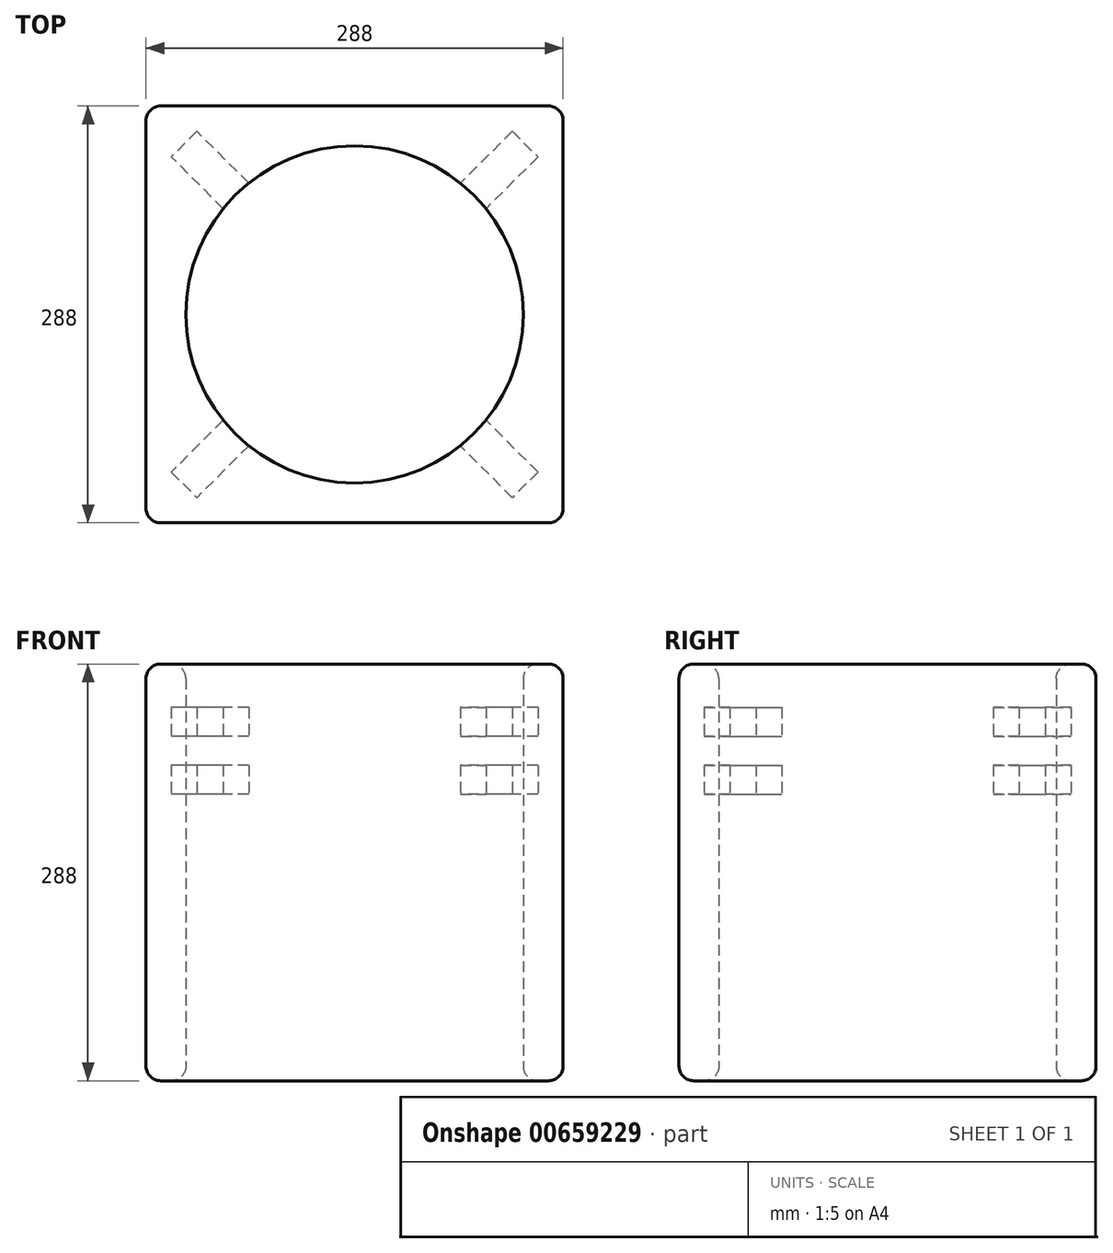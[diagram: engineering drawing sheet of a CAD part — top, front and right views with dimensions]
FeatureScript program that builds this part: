
annotation { "Feature Type Name" : "Feature", "Feature Type Description" : "" }
export const myFeature = defineFeature(function(context is Context, id is Id, definition is map)
    precondition{}
    {
        {
            var Q0;
            Q0=qCreatedBy(makeId("Top.planeOp"),FACE);
            var sketch = newSketch(context, id + "F0", { "sketchPlane" : qUnion([Q0])});
            skCircle(sketch, "E0", {"center": v(0, 0) * mm, "radius": 116.5 * mm});
            skLineSegment(sketch, "E1.bottom", {"start": v(144, 144) * mm, "end": v(-144, 144) * mm});
            skLineSegment(sketch, "E1.top", {"start": v(144, -144) * mm, "end": v(-144, -144) * mm});
            skLineSegment(sketch, "E1.left", {"start": v(144, 144) * mm, "end": v(144, -144) * mm});
            skLineSegment(sketch, "E1.right", {"start": v(-144, 144) * mm, "end": v(-144, -144) * mm});
            skSolve(sketch);
        }
        {
            var Q0;
            Q0=makeQuery(id+"F0.imprint","IMPRINT",FACE,{"disambiguationData":[TD([[makeQuery(id+"F0.imprint","IMPRINT",EDGE,{"derivedFrom":sQuery(id+"F0.wireOp",EDGE,"E0")}),-1.0]])]});
            extrude(context, id + "F1", {"entities" : qUnion([Q0]), "depth" : 288 * mm, "offsetDistance" : 25 * mm});
        }
        {
            var Q0;
            Q0=makeQuery(id+"F1.opExtrude","CAP_FACE",FACE,{"disambiguationData":[OSD([sQuery(id+"F0.wireOp",EDGE,"E0"),sQuery(id+"F0.wireOp",EDGE,"E1.bottom"),sQuery(id+"F0.wireOp",EDGE,"E1.top"),sQuery(id+"F0.wireOp",EDGE,"E1.left"),sQuery(id+"F0.wireOp",EDGE,"E1.right")])],"isStart":false});
            var Q1;
            Q1=makeQuery(id+"F1.opExtrude","CAP_FACE",FACE,{"disambiguationData":[OSD([sQuery(id+"F0.wireOp",EDGE,"E0"),sQuery(id+"F0.wireOp",EDGE,"E1.bottom"),sQuery(id+"F0.wireOp",EDGE,"E1.top"),sQuery(id+"F0.wireOp",EDGE,"E1.left"),sQuery(id+"F0.wireOp",EDGE,"E1.right")])],"isStart":true});
            var Q2;
            {var subQ0=sQuery(id+"F0.wireOp",EDGE,"E1.bottom");Q2=makeQuery(id+"Fkc3ZmtWVtNshut_1.opChamfer","BLEND_EDGE",EDGE,{"blendedFrom":[makeQuery(id+"F1.opExtrude","SWEPT_EDGE",EDGE,{"disambiguationData":[OSD([subQ0,sQuery(id+"F0.wireOp",EDGE,"E1.right")])]}),makeQuery(id+"F1.opExtrude","SWEPT_FACE",FACE,{"disambiguationData":[OSD([subQ0])]})],"blendedInto":[makeQuery(id+"F1.opExtrude","SWEPT_FACE",FACE,{"disambiguationData":[OSD([subQ0])]})]});}
            var Q3;
            Q3=makeQuery(id+"F1.opExtrude","SWEPT_FACE",FACE,{"disambiguationData":[OSD([sQuery(id+"F0.wireOp",EDGE,"E1.right")])]});
            var Q4;
            {var subQ0=sQuery(id+"F0.wireOp",EDGE,"E1.top");Q4=makeQuery(id+"Fkc3ZmtWVtNshut_1.opChamfer","BLEND_EDGE",EDGE,{"blendedFrom":[makeQuery(id+"F1.opExtrude","SWEPT_EDGE",EDGE,{"disambiguationData":[OSD([subQ0,sQuery(id+"F0.wireOp",EDGE,"E1.right")])]}),makeQuery(id+"F1.opExtrude","SWEPT_FACE",FACE,{"disambiguationData":[OSD([subQ0])]})],"blendedInto":[makeQuery(id+"F1.opExtrude","SWEPT_FACE",FACE,{"disambiguationData":[OSD([subQ0])]})]});}
            var Q5;
            {var subQ0=sQuery(id+"F0.wireOp",EDGE,"E1.top");Q5=makeQuery(id+"Fkc3ZmtWVtNshut_1.opChamfer","BLEND_EDGE",EDGE,{"blendedFrom":[makeQuery(id+"F1.opExtrude","SWEPT_EDGE",EDGE,{"disambiguationData":[OSD([subQ0,sQuery(id+"F0.wireOp",EDGE,"E1.left")])]}),makeQuery(id+"F1.opExtrude","SWEPT_FACE",FACE,{"disambiguationData":[OSD([subQ0])]})],"blendedInto":[makeQuery(id+"F1.opExtrude","SWEPT_FACE",FACE,{"disambiguationData":[OSD([subQ0])]})]});}
            var Q6;
            Q6=makeQuery(id+"Fkc3ZmtWVtNshut_1.opChamfer","BLEND_FACE",FACE,{"disambiguationData":[OSD([sQuery(id+"F0.wireOp",EDGE,"E1.top"),sQuery(id+"F0.wireOp",EDGE,"E1.left")])]});
            var Q7;
            Q7=makeQuery(id+"F1.opExtrude","SWEPT_FACE",FACE,{"disambiguationData":[OSD([sQuery(id+"F0.wireOp",EDGE,"E1.left")])]});
            var Q8;
            Q8=makeQuery(id+"Fkc3ZmtWVtNshut_1.opChamfer","BLEND_FACE",FACE,{"disambiguationData":[OSD([sQuery(id+"F0.wireOp",EDGE,"E1.bottom"),sQuery(id+"F0.wireOp",EDGE,"E1.left")])]});
            fillet(context, id + "F2", {"entities" : qUnion([Q0, Q1, Q2, Q3, Q4, Q5, Q6, Q7, Q8]), "radius" : 10 * mm, "tangentPropagation" : true, "allowEdgeOverflow" : false});
        }
        {
            var Q0;
            {var subQ0=sQuery(id+"F0.wireOp",EDGE,"E1.right");var subQ1=sQuery(id+"F0.wireOp",EDGE,"E1.top");Q0=makeQuery(id+"F2.opFillet","BLEND_VERTEX",VERTEX,{"blendedFrom":[makeQuery(id+"F1.opExtrude","CAP_VERTEX",VERTEX,{"disambiguationData":[OSD([subQ1,subQ0])],"isStart":false}),makeQuery(id+"F1.opExtrude","CAP_EDGE",EDGE,{"disambiguationData":[OSD([subQ1])],"isStart":false}),makeQuery(id+"F1.opExtrude","CAP_EDGE",EDGE,{"disambiguationData":[OSD([subQ0])],"isStart":false}),makeQuery(id+"F1.opExtrude","CAP_FACE",FACE,{"disambiguationData":[OSD([sQuery(id+"F0.wireOp",EDGE,"E0"),sQuery(id+"F0.wireOp",EDGE,"E1.bottom"),subQ1,sQuery(id+"F0.wireOp",EDGE,"E1.left"),subQ0])],"isStart":false})],"blendedInto":[makeQuery(id+"F1.opExtrude","CAP_FACE",FACE,{"disambiguationData":[OSD([sQuery(id+"F0.wireOp",EDGE,"E0"),sQuery(id+"F0.wireOp",EDGE,"E1.bottom"),subQ1,sQuery(id+"F0.wireOp",EDGE,"E1.left"),subQ0])],"isStart":false})]});}
            var Q1;
            {var subQ0=sQuery(id+"F0.wireOp",EDGE,"E1.left");var subQ1=sQuery(id+"F0.wireOp",EDGE,"E1.bottom");Q1=makeQuery(id+"F2.opFillet","BLEND_VERTEX",VERTEX,{"blendedFrom":[makeQuery(id+"F1.opExtrude","CAP_VERTEX",VERTEX,{"disambiguationData":[OSD([subQ1,subQ0])],"isStart":false}),makeQuery(id+"F1.opExtrude","CAP_EDGE",EDGE,{"disambiguationData":[OSD([subQ1])],"isStart":false}),makeQuery(id+"F1.opExtrude","CAP_EDGE",EDGE,{"disambiguationData":[OSD([subQ0])],"isStart":false}),makeQuery(id+"F1.opExtrude","CAP_FACE",FACE,{"disambiguationData":[OSD([sQuery(id+"F0.wireOp",EDGE,"E0"),subQ1,sQuery(id+"F0.wireOp",EDGE,"E1.top"),subQ0,sQuery(id+"F0.wireOp",EDGE,"E1.right")])],"isStart":false})],"blendedInto":[makeQuery(id+"F1.opExtrude","CAP_FACE",FACE,{"disambiguationData":[OSD([sQuery(id+"F0.wireOp",EDGE,"E0"),subQ1,sQuery(id+"F0.wireOp",EDGE,"E1.top"),subQ0,sQuery(id+"F0.wireOp",EDGE,"E1.right")])],"isStart":false})]});}
            var Q2;
            {var subQ0=sQuery(id+"F0.wireOp",EDGE,"E1.left");var subQ1=sQuery(id+"F0.wireOp",EDGE,"E1.bottom");Q2=makeQuery(id+"F2.opFillet","BLEND_VERTEX",VERTEX,{"blendedFrom":[makeQuery(id+"F1.opExtrude","CAP_VERTEX",VERTEX,{"disambiguationData":[OSD([subQ1,subQ0])],"isStart":true}),makeQuery(id+"F1.opExtrude","CAP_EDGE",EDGE,{"disambiguationData":[OSD([subQ1])],"isStart":true}),makeQuery(id+"F1.opExtrude","CAP_EDGE",EDGE,{"disambiguationData":[OSD([subQ0])],"isStart":true}),makeQuery(id+"F1.opExtrude","CAP_FACE",FACE,{"disambiguationData":[OSD([sQuery(id+"F0.wireOp",EDGE,"E0"),subQ1,sQuery(id+"F0.wireOp",EDGE,"E1.top"),subQ0,sQuery(id+"F0.wireOp",EDGE,"E1.right")])],"isStart":true})],"blendedInto":[makeQuery(id+"F1.opExtrude","CAP_FACE",FACE,{"disambiguationData":[OSD([sQuery(id+"F0.wireOp",EDGE,"E0"),subQ1,sQuery(id+"F0.wireOp",EDGE,"E1.top"),subQ0,sQuery(id+"F0.wireOp",EDGE,"E1.right")])],"isStart":true})]});}
            cPlane(context, id + "F3", {"entities" : qUnion([Q0, Q1, Q2]), "cplaneType" : CPlaneType.THREE_POINT, "offset" : 25 * mm, "width" : 150 * mm, "height" : 150 * mm});
        }
        {
            var Q0;
            Q0=qCreatedBy(id+"F3.planeOp",FACE);
            var sketch = newSketch(context, id + "F4", { "sketchPlane" : qUnion([Q0])});
            skLineSegment(sketch, "E2.bottom", {"start": v(12.5, 258) * mm, "end": v(-12.5, 258) * mm});
            skLineSegment(sketch, "E2.top", {"start": v(12.5, 238) * mm, "end": v(-12.5, 238) * mm});
            skLineSegment(sketch, "E2.left", {"start": v(12.5, 258) * mm, "end": v(12.5, 238) * mm});
            skLineSegment(sketch, "E2.right", {"start": v(-12.5, 258) * mm, "end": v(-12.5, 238) * mm});
            skPoint(sketch, "E2.middle", {"position": v(0, 248) * mm});
            skLineSegment(sketch, "E3.bottom", {"start": v(12.5, 218) * mm, "end": v(-12.5, 218) * mm});
            skLineSegment(sketch, "E3.top", {"start": v(12.5, 198) * mm, "end": v(-12.5, 198) * mm});
            skLineSegment(sketch, "E3.left", {"start": v(12.5, 218) * mm, "end": v(12.5, 198) * mm});
            skLineSegment(sketch, "E3.right", {"start": v(-12.5, 218) * mm, "end": v(-12.5, 198) * mm});
            skPoint(sketch, "E3.middle", {"position": v(0, 208) * mm});
            skSolve(sketch);
        }
        {
            var Q0;
            Q0=makeQuery(id+"F4.imprint","IMPRINT",FACE,{"disambiguationData":[TD([[makeQuery(id+"F4.imprint","IMPRINT",EDGE,{"derivedFrom":sQuery(id+"F4.wireOp",EDGE,"E2.bottom")}),1.0]])]});
            var Q1;
            Q1=makeQuery(id+"F4.imprint","IMPRINT",FACE,{"disambiguationData":[TD([[makeQuery(id+"F4.imprint","IMPRINT",EDGE,{"derivedFrom":sQuery(id+"F4.wireOp",EDGE,"E3.bottom")}),1.0]])]});
            extrude(context, id + "F5", {"entities" : qUnion([Q0, Q1]), "operationType" : NewBodyOperationType.REMOVE, "depth" : 333 * mm, "offsetDistance" : 25 * mm, "symmetric" : true});
        }
        {
            var Q0;
            {var subQ0=sQuery(id+"F0.wireOp",EDGE,"E1.left");var subQ1=sQuery(id+"F0.wireOp",EDGE,"E1.top");Q0=makeQuery(id+"F2.opFillet","BLEND_VERTEX",VERTEX,{"blendedFrom":[makeQuery(id+"F1.opExtrude","CAP_VERTEX",VERTEX,{"disambiguationData":[OSD([subQ1,subQ0])],"isStart":false}),makeQuery(id+"F1.opExtrude","CAP_EDGE",EDGE,{"disambiguationData":[OSD([subQ1])],"isStart":false}),makeQuery(id+"F1.opExtrude","CAP_EDGE",EDGE,{"disambiguationData":[OSD([subQ0])],"isStart":false}),makeQuery(id+"F1.opExtrude","CAP_FACE",FACE,{"disambiguationData":[OSD([sQuery(id+"F0.wireOp",EDGE,"E0"),sQuery(id+"F0.wireOp",EDGE,"E1.bottom"),subQ1,subQ0,sQuery(id+"F0.wireOp",EDGE,"E1.right")])],"isStart":false})],"blendedInto":[makeQuery(id+"F1.opExtrude","CAP_FACE",FACE,{"disambiguationData":[OSD([sQuery(id+"F0.wireOp",EDGE,"E0"),sQuery(id+"F0.wireOp",EDGE,"E1.bottom"),subQ1,subQ0,sQuery(id+"F0.wireOp",EDGE,"E1.right")])],"isStart":false})]});}
            var Q1;
            {var subQ0=sQuery(id+"F0.wireOp",EDGE,"E1.right");var subQ1=sQuery(id+"F0.wireOp",EDGE,"E1.bottom");Q1=makeQuery(id+"F2.opFillet","BLEND_VERTEX",VERTEX,{"blendedFrom":[makeQuery(id+"F1.opExtrude","CAP_VERTEX",VERTEX,{"disambiguationData":[OSD([subQ1,subQ0])],"isStart":false}),makeQuery(id+"F1.opExtrude","CAP_EDGE",EDGE,{"disambiguationData":[OSD([subQ1])],"isStart":false}),makeQuery(id+"F1.opExtrude","CAP_EDGE",EDGE,{"disambiguationData":[OSD([subQ0])],"isStart":false}),makeQuery(id+"F1.opExtrude","CAP_FACE",FACE,{"disambiguationData":[OSD([sQuery(id+"F0.wireOp",EDGE,"E0"),subQ1,sQuery(id+"F0.wireOp",EDGE,"E1.top"),sQuery(id+"F0.wireOp",EDGE,"E1.left"),subQ0])],"isStart":false})],"blendedInto":[makeQuery(id+"F1.opExtrude","CAP_FACE",FACE,{"disambiguationData":[OSD([sQuery(id+"F0.wireOp",EDGE,"E0"),subQ1,sQuery(id+"F0.wireOp",EDGE,"E1.top"),sQuery(id+"F0.wireOp",EDGE,"E1.left"),subQ0])],"isStart":false})]});}
            var Q2;
            {var subQ0=sQuery(id+"F0.wireOp",EDGE,"E1.right");var subQ1=sQuery(id+"F0.wireOp",EDGE,"E1.bottom");Q2=makeQuery(id+"F2.opFillet","BLEND_VERTEX",VERTEX,{"blendedFrom":[makeQuery(id+"F1.opExtrude","CAP_VERTEX",VERTEX,{"disambiguationData":[OSD([subQ1,subQ0])],"isStart":true}),makeQuery(id+"F1.opExtrude","CAP_EDGE",EDGE,{"disambiguationData":[OSD([subQ1])],"isStart":true}),makeQuery(id+"F1.opExtrude","CAP_EDGE",EDGE,{"disambiguationData":[OSD([subQ0])],"isStart":true}),makeQuery(id+"F1.opExtrude","CAP_FACE",FACE,{"disambiguationData":[OSD([sQuery(id+"F0.wireOp",EDGE,"E0"),subQ1,sQuery(id+"F0.wireOp",EDGE,"E1.top"),sQuery(id+"F0.wireOp",EDGE,"E1.left"),subQ0])],"isStart":true})],"blendedInto":[makeQuery(id+"F1.opExtrude","CAP_FACE",FACE,{"disambiguationData":[OSD([sQuery(id+"F0.wireOp",EDGE,"E0"),subQ1,sQuery(id+"F0.wireOp",EDGE,"E1.top"),sQuery(id+"F0.wireOp",EDGE,"E1.left"),subQ0])],"isStart":true})]});}
            cPlane(context, id + "F6", {"entities" : qUnion([Q0, Q1, Q2]), "cplaneType" : CPlaneType.THREE_POINT, "offset" : 25 * mm, "width" : 150 * mm, "height" : 150 * mm});
        }
        {
            var Q0;
            Q0=qCreatedBy(id+"F6.planeOp",FACE);
            var sketch = newSketch(context, id + "F7", { "sketchPlane" : qUnion([Q0])});
            skLineSegment(sketch, "E4.bottom", {"start": v(12.5, 258) * mm, "end": v(-12.5, 258) * mm});
            skLineSegment(sketch, "E4.top", {"start": v(12.5, 238) * mm, "end": v(-12.5, 238) * mm});
            skLineSegment(sketch, "E4.left", {"start": v(12.5, 258) * mm, "end": v(12.5, 238) * mm});
            skLineSegment(sketch, "E4.right", {"start": v(-12.5, 258) * mm, "end": v(-12.5, 238) * mm});
            skPoint(sketch, "E4.middle", {"position": v(0, 248) * mm});
            skLineSegment(sketch, "E5.bottom", {"start": v(12.5, 218) * mm, "end": v(-12.5, 218) * mm});
            skLineSegment(sketch, "E5.top", {"start": v(12.5, 198) * mm, "end": v(-12.5, 198) * mm});
            skLineSegment(sketch, "E5.left", {"start": v(12.5, 218) * mm, "end": v(12.5, 198) * mm});
            skLineSegment(sketch, "E5.right", {"start": v(-12.5, 218) * mm, "end": v(-12.5, 198) * mm});
            skPoint(sketch, "E5.middle", {"position": v(0, 208) * mm});
            skSolve(sketch);
        }
        {
            var Q0;
            Q0=makeQuery(id+"F7.imprint","IMPRINT",FACE,{"disambiguationData":[TD([[makeQuery(id+"F7.imprint","IMPRINT",EDGE,{"derivedFrom":sQuery(id+"F7.wireOp",EDGE,"E4.bottom")}),1.0]])]});
            var Q1;
            Q1=makeQuery(id+"F7.imprint","IMPRINT",FACE,{"disambiguationData":[TD([[makeQuery(id+"F7.imprint","IMPRINT",EDGE,{"derivedFrom":sQuery(id+"F7.wireOp",EDGE,"E5.bottom")}),1.0]])]});
            extrude(context, id + "F8", {"entities" : qUnion([Q0, Q1]), "operationType" : NewBodyOperationType.REMOVE, "depth" : 333 * mm, "offsetDistance" : 25 * mm, "symmetric" : true});
        }
    });
